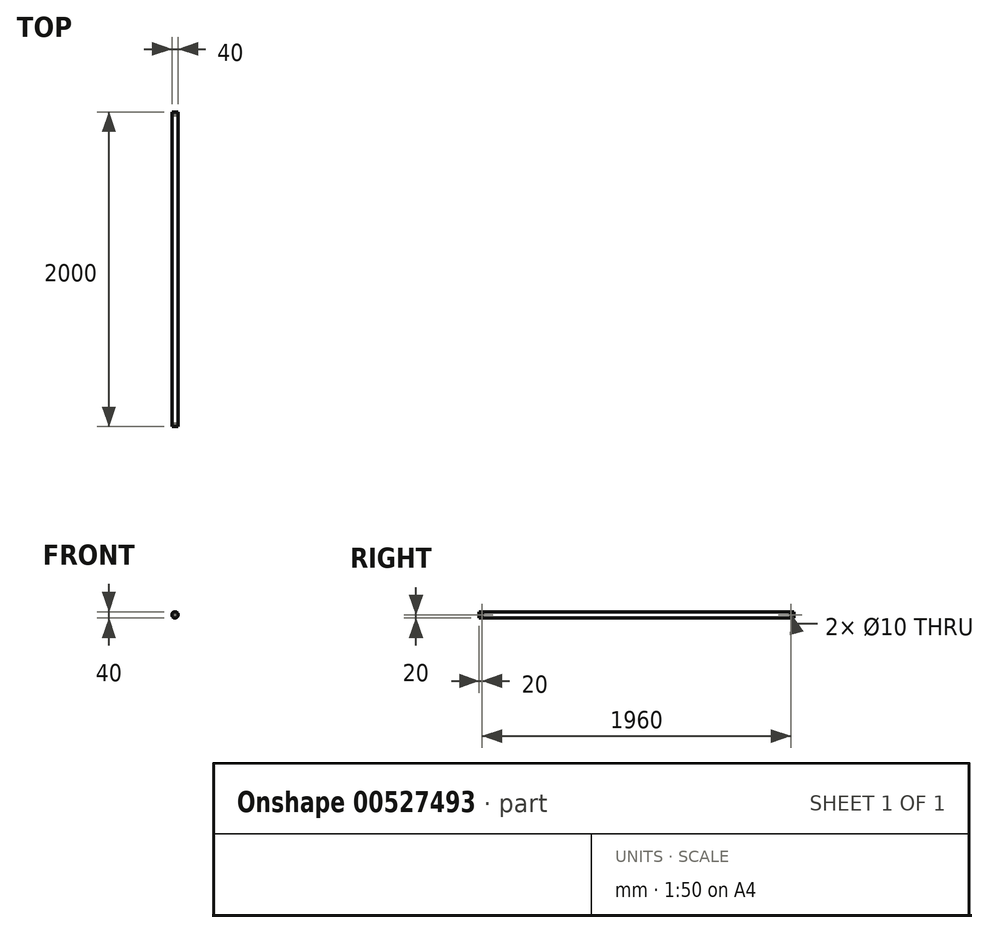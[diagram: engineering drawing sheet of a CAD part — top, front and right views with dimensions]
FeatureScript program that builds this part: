
annotation { "Feature Type Name" : "Feature", "Feature Type Description" : "" }
export const myFeature = defineFeature(function(context is Context, id is Id, definition is map)
    precondition{}
    {
        {
            var Q0;
            Q0=qCreatedBy(makeId("Front.planeOp"),FACE);
            var sketch = newSketch(context, id + "F0", { "sketchPlane" : qUnion([Q0])});
            skCircle(sketch, "E0", {"center": v(0, 0) * mm, "radius": 20 * mm});
            skSolve(sketch);
        }
        {
            var Q0;
            Q0 = qSketchRegion(id + "F0", true);
            extrude(context, id + "F1", {"entities" : qUnion([Q0]), "depth" : 2000 * mm, "offsetDistance" : 25 * mm});
        }
        {
            var Q0;
            Q0=qCreatedBy(makeId("Right.planeOp"),FACE);
            var sketch = newSketch(context, id + "F2", { "sketchPlane" : qUnion([Q0])});
            skLineSegment(sketch, "E1", {"start": v(0, 0) * mm, "end": v(-1000.95, 0) * mm, "construction": true});
            skPoint(sketch, "E2", {"position": v(-20, 0) * mm});
            skPoint(sketch, "E3", {"position": v(-1980, 0) * mm});
            skSolve(sketch);
        }
        {
            var Q0;
            Q0=sQuery(id+"F2.wireOp",VERTEX,"E3");
            var Q1;
            Q1=makeQuery(id+"F1.opExtrude","SWEPT_BODY",BODY,{"disambiguationData":[OSD([sQuery(id+"F0.wireOp",EDGE,"E0")])]});
            hole(context, id + "F3", {"style" : HoleStyle.SIMPLE, "endStyle" : HoleEndStyle.THROUGH, "holeDiameter" : 10 * mm, "isTappedThrough" : true, "tappedDepth" : 12 * mm, "tapClearance" : 3, "startFromSketch" : true, "locations" : qUnion([Q0]), "scope" : qUnion([Q1])});
        }
        {
            var Q0;
            Q0=sQuery(id+"F2.wireOp",VERTEX,"E3");
            var Q1;
            Q1=makeQuery(id+"F1.opExtrude","SWEPT_BODY",BODY,{"disambiguationData":[OSD([sQuery(id+"F0.wireOp",EDGE,"E0")])]});
            hole(context, id + "F4", {"style" : HoleStyle.SIMPLE, "endStyle" : HoleEndStyle.THROUGH, "oppositeDirection" : true, "holeDiameter" : 10 * mm, "isTappedThrough" : true, "tappedDepth" : 12 * mm, "tapClearance" : 3, "startFromSketch" : true, "locations" : qUnion([Q0]), "scope" : qUnion([Q1])});
        }
        {
            var Q0;
            Q0=sQuery(id+"F2.wireOp",VERTEX,"E2");
            var Q1;
            Q1=makeQuery(id+"F1.opExtrude","SWEPT_BODY",BODY,{"disambiguationData":[OSD([sQuery(id+"F0.wireOp",EDGE,"E0")])]});
            hole(context, id + "F5", {"style" : HoleStyle.SIMPLE, "endStyle" : HoleEndStyle.THROUGH, "holeDiameter" : 10 * mm, "isTappedThrough" : true, "tappedDepth" : 12 * mm, "tapClearance" : 3, "startFromSketch" : true, "locations" : qUnion([Q0]), "scope" : qUnion([Q1])});
        }
        {
            var Q0;
            Q0=sQuery(id+"F2.wireOp",VERTEX,"E2");
            var Q1;
            Q1=makeQuery(id+"F1.opExtrude","SWEPT_BODY",BODY,{"disambiguationData":[OSD([sQuery(id+"F0.wireOp",EDGE,"E0")])]});
            hole(context, id + "F6", {"style" : HoleStyle.SIMPLE, "endStyle" : HoleEndStyle.THROUGH, "oppositeDirection" : true, "holeDiameter" : 10 * mm, "isTappedThrough" : true, "tappedDepth" : 12 * mm, "tapClearance" : 3, "startFromSketch" : true, "locations" : qUnion([Q0]), "scope" : qUnion([Q1])});
        }
    });
